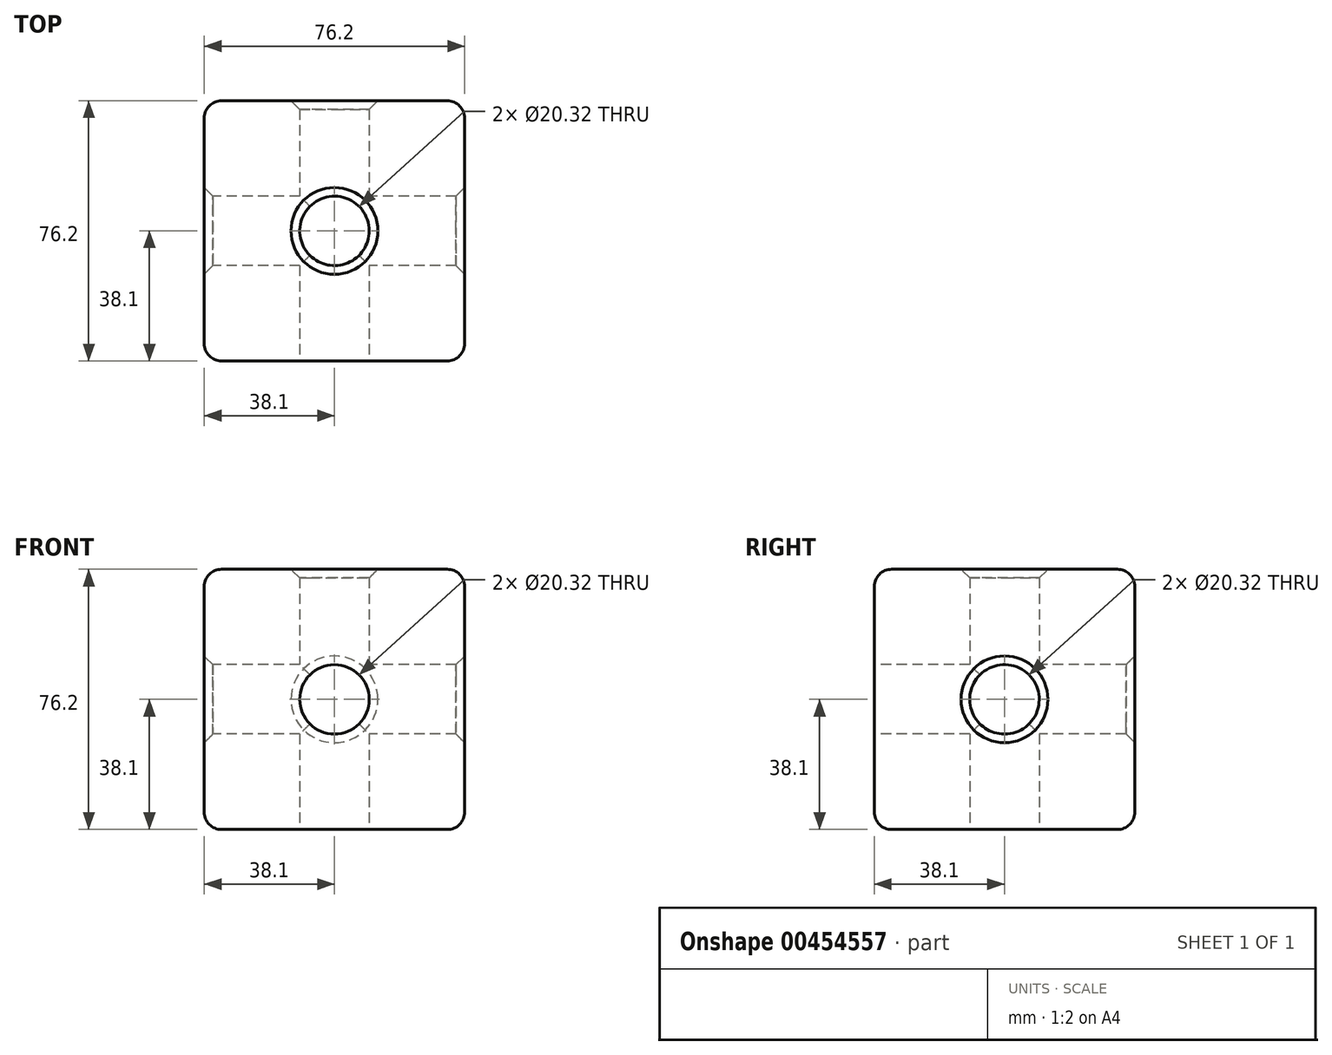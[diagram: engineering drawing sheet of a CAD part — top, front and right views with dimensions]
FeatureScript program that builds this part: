
annotation { "Feature Type Name" : "Feature", "Feature Type Description" : "" }
export const myFeature = defineFeature(function(context is Context, id is Id, definition is map)
    precondition{}
    {
        {
            var Q0;
            Q0=qCreatedBy(makeId("Top.planeOp"),FACE);
            var sketch = newSketch(context, id + "F0", { "sketchPlane" : qUnion([Q0])});
            skLineSegment(sketch, "E0.bottom", {"start": v(-38.1, 38.1) * mm, "end": v(38.1, 38.1) * mm});
            skLineSegment(sketch, "E0.top", {"start": v(-38.1, -38.1) * mm, "end": v(38.1, -38.1) * mm});
            skLineSegment(sketch, "E0.left", {"start": v(-38.1, 38.1) * mm, "end": v(-38.1, -38.1) * mm});
            skLineSegment(sketch, "E0.right", {"start": v(38.1, 38.1) * mm, "end": v(38.1, -38.1) * mm});
            skPoint(sketch, "E0.middle", {"position": v(0, 0) * mm});
            skSolve(sketch);
        }
        {
            var Q0;
            Q0 = qSketchRegion(id + "F0", true);
            extrude(context, id + "F1", {"entities" : qUnion([Q0]), "endBound" : BoundingType.SYMMETRIC, "depth" : 76.2 * mm});
        }
        {
            var Q0;
            Q0=makeQuery(id+"F1.opExtrude","SWEPT_FACE",FACE,{"disambiguationData":[OSD([sQuery(id+"F0.wireOp",EDGE,"E0.left")])]});
            var sketch = newSketch(context, id + "F2", { "sketchPlane" : qUnion([Q0])});
            skCircle(sketch, "E1", {"center": v(0, 0) * mm, "radius": 10.16 * mm});
            skSolve(sketch);
        }
        {
            var Q0;
            Q0 = qSketchRegion(id + "F2", true);
            extrude(context, id + "F3", {"entities" : qUnion([Q0]), "operationType" : NewBodyOperationType.REMOVE, "endBound" : BoundingType.SYMMETRIC, "oppositeDirection" : true, "depth" : 294.64 * mm});
        }
        {
            var Q0;
            Q0=makeQuery(id+"F1.opExtrude","CAP_FACE",FACE,{"disambiguationData":[OSD([sQuery(id+"F0.wireOp",EDGE,"E0.bottom"),sQuery(id+"F0.wireOp",EDGE,"E0.top"),sQuery(id+"F0.wireOp",EDGE,"E0.left"),sQuery(id+"F0.wireOp",EDGE,"E0.right")])],"isStart":true});
            var sketch = newSketch(context, id + "F4", { "sketchPlane" : qUnion([Q0])});
            skCircle(sketch, "E2", {"center": v(0, 0) * mm, "radius": 10.16 * mm});
            skSolve(sketch);
        }
        {
            var Q0;
            Q0 = qSketchRegion(id + "F4", true);
            extrude(context, id + "F5", {"entities" : qUnion([Q0]), "operationType" : NewBodyOperationType.REMOVE, "oppositeDirection" : true, "depth" : 163.32 * mm});
        }
        {
            var Q0;
            Q0=makeQuery(id+"F1.opExtrude","SWEPT_FACE",FACE,{"disambiguationData":[OSD([sQuery(id+"F0.wireOp",EDGE,"E0.top")])]});
            var sketch = newSketch(context, id + "F6", { "sketchPlane" : qUnion([Q0])});
            skCircle(sketch, "E3", {"center": v(0, 0) * mm, "radius": 10.16 * mm});
            skSolve(sketch);
        }
        {
            var Q0;
            Q0 = qSketchRegion(id + "F6", true);
            extrude(context, id + "F7", {"entities" : qUnion([Q0]), "operationType" : NewBodyOperationType.REMOVE, "oppositeDirection" : true, "depth" : 99.06 * mm});
        }
        {
            var Q0;
            Q0=makeQuery(id+"F1.opExtrude","CAP_EDGE",EDGE,{"disambiguationData":[OSD([sQuery(id+"F0.wireOp",EDGE,"E0.left")])],"isStart":false});
            var Q1;
            Q1=makeQuery(id+"F1.opExtrude","SWEPT_EDGE",EDGE,{"disambiguationData":[OSD([sQuery(id+"F0.wireOp",EDGE,"E0.top"),sQuery(id+"F0.wireOp",EDGE,"E0.left")])]});
            var Q2;
            Q2=makeQuery(id+"F1.opExtrude","SWEPT_EDGE",EDGE,{"disambiguationData":[OSD([sQuery(id+"F0.wireOp",EDGE,"E0.bottom"),sQuery(id+"F0.wireOp",EDGE,"E0.left")])]});
            var Q3;
            Q3=makeQuery(id+"F1.opExtrude","CAP_EDGE",EDGE,{"disambiguationData":[OSD([sQuery(id+"F0.wireOp",EDGE,"E0.left")])],"isStart":true});
            var Q4;
            Q4=makeQuery(id+"F1.opExtrude","CAP_EDGE",EDGE,{"disambiguationData":[OSD([sQuery(id+"F0.wireOp",EDGE,"E0.bottom")])],"isStart":true});
            var Q5;
            Q5=makeQuery(id+"F1.opExtrude","CAP_EDGE",EDGE,{"disambiguationData":[OSD([sQuery(id+"F0.wireOp",EDGE,"E0.top")])],"isStart":true});
            var Q6;
            Q6=makeQuery(id+"F1.opExtrude","CAP_EDGE",EDGE,{"disambiguationData":[OSD([sQuery(id+"F0.wireOp",EDGE,"E0.bottom")])],"isStart":false});
            var Q7;
            Q7=makeQuery(id+"F1.opExtrude","CAP_EDGE",EDGE,{"disambiguationData":[OSD([sQuery(id+"F0.wireOp",EDGE,"E0.top")])],"isStart":false});
            var Q8;
            Q8=makeQuery(id+"F1.opExtrude","SWEPT_EDGE",EDGE,{"disambiguationData":[OSD([sQuery(id+"F0.wireOp",EDGE,"E0.top"),sQuery(id+"F0.wireOp",EDGE,"E0.right")])]});
            var Q9;
            Q9=makeQuery(id+"F1.opExtrude","CAP_EDGE",EDGE,{"disambiguationData":[OSD([sQuery(id+"F0.wireOp",EDGE,"E0.right")])],"isStart":true});
            var Q10;
            Q10=makeQuery(id+"F1.opExtrude","SWEPT_EDGE",EDGE,{"disambiguationData":[OSD([sQuery(id+"F0.wireOp",EDGE,"E0.bottom"),sQuery(id+"F0.wireOp",EDGE,"E0.right")])]});
            var Q11;
            Q11=makeQuery(id+"F1.opExtrude","CAP_EDGE",EDGE,{"disambiguationData":[OSD([sQuery(id+"F0.wireOp",EDGE,"E0.right")])],"isStart":false});
            fillet(context, id + "F8", {"entities" : qUnion([Q0, Q1, Q2, Q3, Q4, Q5, Q6, Q7, Q8, Q9, Q10, Q11]), "radius" : 5.08 * mm, "tangentPropagation" : true, "allowEdgeOverflow" : false});
        }
        {
            var Q0;
            Q0=makeQuery(id+"F5.boolean.opBoolean","COPY",EDGE,{"derivedFrom":makeQuery(id+"F5.opExtrude","CAP_EDGE",EDGE,{"disambiguationData":[OSD([sQuery(id+"F4.wireOp",EDGE,"E2")])],"isStart":true})});
            var Q1;
            Q1=makeQuery(id+"F3.boolean.opBoolean","INTERSECT",EDGE,{"derivedFrom":[makeQuery(id+"F1.opExtrude","SWEPT_FACE",FACE,{"disambiguationData":[OSD([sQuery(id+"F0.wireOp",EDGE,"E0.right")])]}),makeQuery(id+"F3.opExtrude","SWEPT_FACE",FACE,{"disambiguationData":[OSD([sQuery(id+"F2.wireOp",EDGE,"E1")])]})]});
            var Q2;
            Q2=makeQuery(id+"F7.boolean.opBoolean","COPY",EDGE,{"derivedFrom":makeQuery(id+"F7.opExtrude","CAP_EDGE",EDGE,{"disambiguationData":[OSD([sQuery(id+"F6.wireOp",EDGE,"E3")])],"isStart":true})});
            var Q3;
            Q3=makeQuery(id+"F7.boolean.opBoolean","INTERSECT",EDGE,{"derivedFrom":[makeQuery(id+"F1.opExtrude","SWEPT_FACE",FACE,{"disambiguationData":[OSD([sQuery(id+"F0.wireOp",EDGE,"E0.bottom")])]}),makeQuery(id+"F7.opExtrude","SWEPT_FACE",FACE,{"disambiguationData":[OSD([sQuery(id+"F6.wireOp",EDGE,"E3")])]})]});
            var Q4;
            Q4=makeQuery(id+"F5.boolean.opBoolean","INTERSECT",EDGE,{"derivedFrom":[makeQuery(id+"F1.opExtrude","CAP_FACE",FACE,{"disambiguationData":[OSD([sQuery(id+"F0.wireOp",EDGE,"E0.bottom"),sQuery(id+"F0.wireOp",EDGE,"E0.top"),sQuery(id+"F0.wireOp",EDGE,"E0.left"),sQuery(id+"F0.wireOp",EDGE,"E0.right")])],"isStart":false}),makeQuery(id+"F5.opExtrude","SWEPT_FACE",FACE,{"disambiguationData":[OSD([sQuery(id+"F4.wireOp",EDGE,"E2")])]})]});
            var Q5;
            Q5=makeQuery(id+"F3.boolean.opBoolean","INTERSECT",EDGE,{"derivedFrom":[makeQuery(id+"F1.opExtrude","SWEPT_FACE",FACE,{"disambiguationData":[OSD([sQuery(id+"F0.wireOp",EDGE,"E0.left")])]}),makeQuery(id+"F3.opExtrude","SWEPT_FACE",FACE,{"disambiguationData":[OSD([sQuery(id+"F2.wireOp",EDGE,"E1")])]})]});
            chamfer(context, id + "F9", {"entities" : qUnion([Q0, Q1, Q2, Q3, Q4, Q5]), "width" : 2.54 * mm, "tangentPropagation" : true});
        }
    });
